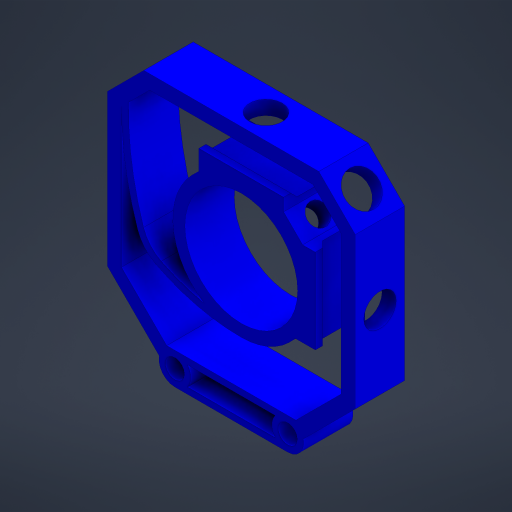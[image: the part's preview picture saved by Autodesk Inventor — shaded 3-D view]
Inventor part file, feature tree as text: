
AUTODESK INVENTOR PART (.ipt)
format: ipt  version: 2023.4 (Build 274418000, 418)  size: 432,128 bytes
history: native  units: mm
features: extrude x6, projected_geometry x4, reference x4, other x3, plane x1, mirror x1, sketch x1
ambient origin geometry x8: Origin, YZ Plane, XZ Plane, XY Plane, X Axis, Y Axis, Z Axis, Center Point
bodies: Solid1 (feature_tree)
feature tree (20):
  extrude  "Extrusion1"  TaperAngle=45.0deg  [1 undecoded]
  extrude  "Extrusion2"  Depth=10.0mm
  extrude  "Extrusion3"  Depth=10.0mm
  extrude  "Extrusion4"  Depth=10.0mm
  plane  "Work Plane1"
  mirror  "Mirror1"
  extrude  "Extrusion5"  Depth=10.0mm
  extrude  "Extrusion6"  Depth=10.0mm
  sketch  "Sketch1"  dims[d2=2.5mm d3=45.0deg d4=20.0mm d5=2.5mm d6=2.125mm d7=1.0mm d8=15.0mm d9=4.0mm d10=0.625mm d11=5.0mm d12=135.0deg d13=3.0mm d14=2.0mm d15=2.0mm d16=38.935534mm d17=38.935534mm d18=9.25mm d19=9.25mm d20=9.25mm d21=9.25mm d22=5.0mm d23=5.0mm d24=5.0mm d25=5.0mm d26=2.5mm d28=8.75mm d29=0.0mm d30=1.875mm d31=1.25mm d32=0.0mm d33=5.75mm d34=10.0mm d35=0.0mm d36=1.25mm d37=135.0deg d38=10.0mm d39=0.0mm d40=3.75mm d41=6.0mm d42=10.0mm d43=0.0mm d44=10.0mm d45=0.0mm d48=17.5mm d49=5.0mm d50=1.25mm d51=2.5mm d52=2.5mm d56=0.1425mm d57=0.1425mm d58=1.25mm d59=1.25mm d53=0.5mm d54=0.872665mm d55=0.5mm]
  projected_geometry  "Projected Loop1"
  projected_geometry  "Projected Loop2"
  projected_geometry  "Projected Loop3"
  projected_geometry  "Projected Loop4"
  reference  "Reference4"
  reference  "Reference5"
  reference  "Reference6"
  reference  "Reference7"
  other  "<path>\Projects\Project Protocube\Protocube\CAD, STL, OBJ Files\1 CAD\Cube 1x1 V5.iam"
  other  "Cube 1x1 V5.iam"
  other  "Cube 1x1 Bottom V5 Closed Slotted:1"
note: 1 required parameter value undecoded (feature->parameter linkage not recoverable at this tier; creation-order binding heuristic only, values carry confidence <= 0.55)
note: 1 file-system path scrubbed to <path> (originals preserved in map.json)
